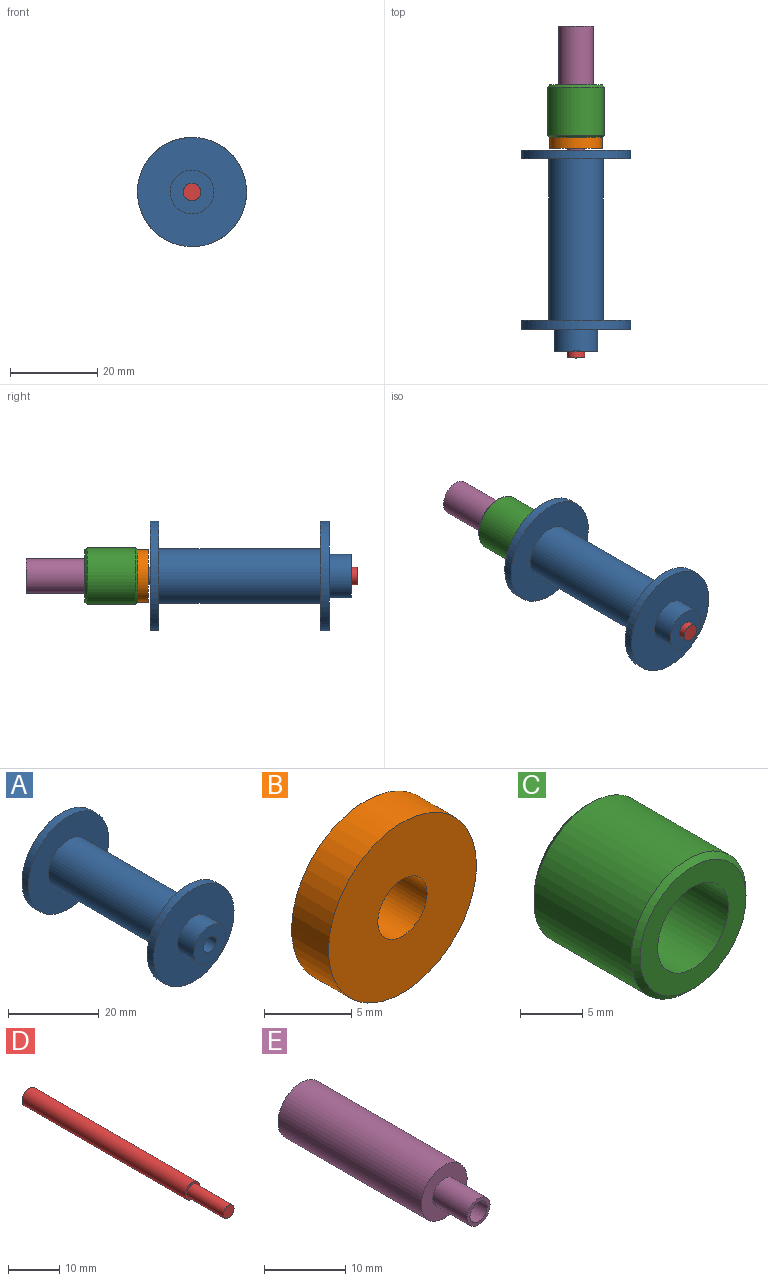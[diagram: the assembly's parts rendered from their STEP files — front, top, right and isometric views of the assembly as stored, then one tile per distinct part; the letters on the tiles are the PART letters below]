
ASSEMBLY  parts=5 mates=4
PART A: 10 faces, bbox 25x46x25 mm
  f0: cylinder r=6.25mm len=37mm, axis (0,1,0), area 1453mm2, adj f3,f6
  f1: cylinder r=12.5mm len=25mm, axis (0,1,0), area 157.1mm2, adj f2,f3
  f2: plane 25x25mm, normal (0,-1,0), area 412.3mm2, adj f1,f8
  f3: plane 25x25mm, normal (0,1,0), area 368.2mm2, adj f0,f1
  f4: cylinder r=12.5mm len=25mm, axis (0,-1,0), area 157.1mm2, adj f5,f6
  f5: plane 25x25mm, normal (0,1,0), area 478.3mm2, adj f4,f7
  f6: plane 25x25mm, normal (0,-1,0), area 368.2mm2, adj f0,f4
  f7: cylinder r=2mm len=46mm, axis (0,1,0), area 578.1mm2, adj f5,f9
  f8: cylinder r=5mm len=10mm, axis (0,1,0), area 157.1mm2, adj f2,f9
  f9: plane 10x10mm, normal (0,-1,0), area 66mm2, adj f7,f8
PART B: 4 faces, bbox 12x3x12 mm
  f0: cylinder r=2mm len=4mm, axis (0,1,0), area 37.7mm2, adj f2,f3
  f1: cylinder r=6mm len=12mm, axis (0,1,0), area 113.1mm2, adj f2,f3
  f2: plane 12x12mm, normal (0,-1,0), area 100.5mm2, adj f0,f1
  f3: plane 12x12mm, normal (0,1,0), area 100.5mm2, adj f0,f1
PART C: 6 faces, bbox 13x12x13 mm
  f0: cylinder r=4mm len=12mm, axis (0,1,0), area 301.6mm2, adj f2,f3
  f1: cylinder r=6.5mm len=13mm, axis (0,1,0), area 449.2mm2, adj f4,f5
  f2: plane 12x12mm, normal (0,-1,0), area 62.8mm2, adj f0,f4
  f3: plane 12x12mm, normal (0,1,0), area 62.8mm2, adj f0,f5
  f4: cone r=6mm half-angle=45deg, axis (0,1,0), area 27.8mm2, adj f1,f2
  f5: cone r=6.5mm half-angle=45deg, axis (0,-1,0), area 27.8mm2, adj f1,f3
PART D: 5 faces, bbox 4x55x4 mm
  f0: cylinder r=2mm len=45mm, axis (0,1,0), area 565.5mm2, adj f1,f2
  f1: plane 4x4mm, normal (0,-1,0), area 5.5mm2, adj f0,f3
  f2: plane 4x4mm, normal (0,1,0), area 12.6mm2, adj f0
  f3: cylinder r=1.5mm len=10mm, axis (0,1,0), area 94.2mm2, adj f1,f4
  f4: plane 3x3mm, normal (0,-1,0), area 7.1mm2, adj f3
PART E: 7 faces, bbox 8x31x8 mm
  f0: cylinder r=4mm len=25mm, axis (0,1,0), area 628.3mm2, adj f1,f2
  f1: plane 8x8mm, normal (0,-1,0), area 37.7mm2, adj f0,f3
  f2: plane 8x8mm, normal (0,1,0), area 50.3mm2, adj f0
  f3: cylinder r=2mm len=6mm, axis (0,1,0), area 75.4mm2, adj f1,f4
  f4: plane 4x4mm, normal (0,-1,0), area 5.5mm2, adj f3,f5
  f5: cylinder r=1.5mm len=10mm, axis (0,-1,0), area 94.2mm2, adj f4,f6
  f6: plane 3x3mm, normal (0,-1,0), area 7.1mm2, adj f5
PLACE A rot(axis=(0,1,0),41.7deg) t=(0,-16.91,0)mm
PLACE B t=(0,-11.5,0)mm
PLACE C at identity fixed
PLACE D rot(axis=(1,0,0),180deg) t=(0,-62.5,0)mm
PLACE E t=(0,13.5,0)mm
MATE fastened B.f0 <-> E.f3  axis (0,1,0) through (0,-11.5,0)mm
MATE fastened D.f3 <-> E.f5  axis (0,-1,0) through (0,-17.5,0)mm
MATE revolute B.f1 <-> C.f1  axis (0,1,0) through (0,-11.5,0)mm
MATE cylindrical A.f4 <-> E.f3  axis (0,1,0) through (0,-14.91,0)mm
